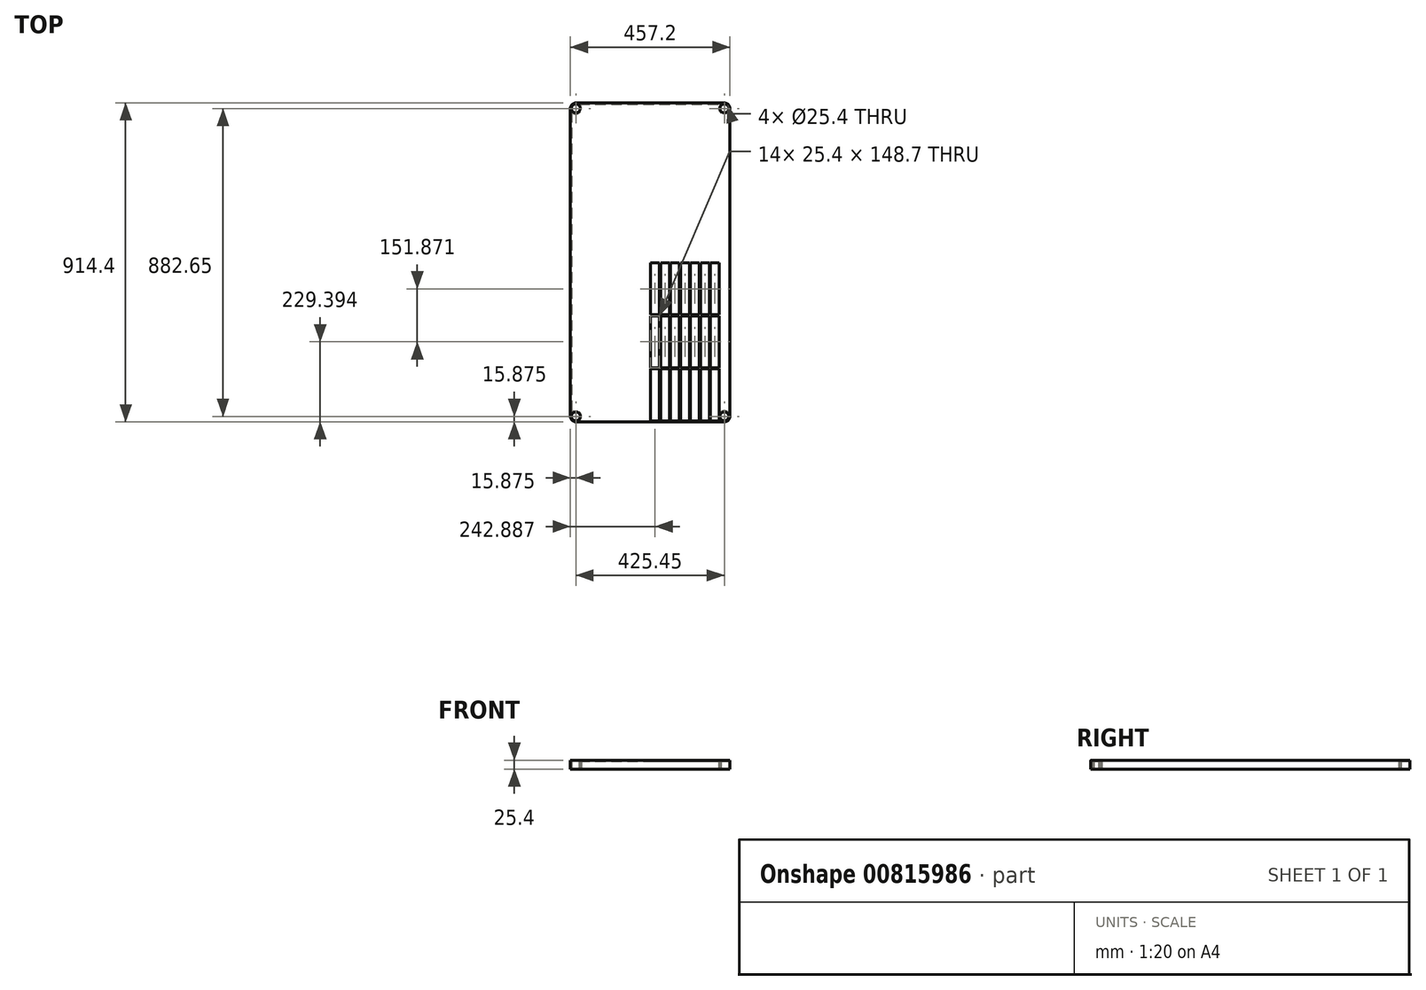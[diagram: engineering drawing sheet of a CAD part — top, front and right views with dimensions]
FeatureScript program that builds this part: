
annotation { "Feature Type Name" : "Feature", "Feature Type Description" : "" }
export const myFeature = defineFeature(function(context is Context, id is Id, definition is map)
    precondition{}
    {
        {
            var Q0;
            Q0=qCreatedBy(makeId("Top.planeOp"),FACE);
            var sketch = newSketch(context, id + "F0", { "sketchPlane" : qUnion([Q0])});
            skLineSegment(sketch, "E0.bottom", {"start": v(-212.73, 457.2) * mm, "end": v(212.72, 457.2) * mm});
            skLineSegment(sketch, "E0.top", {"start": v(-212.73, -457.2) * mm, "end": v(212.73, -457.2) * mm});
            skLineSegment(sketch, "E0.left", {"start": v(-228.6, 441.32) * mm, "end": v(-228.6, -441.33) * mm});
            skLineSegment(sketch, "E0.right", {"start": v(228.6, 441.33) * mm, "end": v(228.6, -441.33) * mm});
            skLineSegment(sketch, "E1", {"start": v(-228.6, 457.2) * mm, "end": v(228.6, -457.2) * mm, "construction": true});
            skPoint(sketch, "E2.visualSharp", {"position": v(-228.6, -457.2) * mm});
            skArc(sketch, "E2.filletArc", {"start": v(-228.6, -441.33) * mm, "mid": v(-223.95, -452.55) * mm, "end": v(-212.73, -457.2) * mm});
            skPoint(sketch, "E3.visualSharp", {"position": v(-228.6, 457.2) * mm});
            skArc(sketch, "E3.filletArc", {"start": v(-212.73, 457.2) * mm, "mid": v(-223.95, 452.55) * mm, "end": v(-228.6, 441.32) * mm});
            skPoint(sketch, "E4.visualSharp", {"position": v(228.6, 457.2) * mm});
            skArc(sketch, "E4.filletArc", {"start": v(228.6, 441.33) * mm, "mid": v(223.95, 452.55) * mm, "end": v(212.72, 457.2) * mm});
            skPoint(sketch, "E5.visualSharp", {"position": v(228.6, -457.2) * mm});
            skArc(sketch, "E5.filletArc", {"start": v(212.73, -457.2) * mm, "mid": v(223.95, -452.55) * mm, "end": v(228.6, -441.33) * mm});
            skCircle(sketch, "E6", {"center": v(-212.73, -441.33) * mm, "radius": 12.7 * mm});
            skCircle(sketch, "E7", {"center": v(212.73, -441.33) * mm, "radius": 12.7 * mm});
            skCircle(sketch, "E8", {"center": v(-212.73, 441.32) * mm, "radius": 12.7 * mm});
            skCircle(sketch, "E9", {"center": v(212.72, 441.33) * mm, "radius": 12.7 * mm});
            skSolve(sketch);
        }
        {
            var Q0;
            Q0=makeQuery(id+"F0.imprint","IMPRINT",FACE,{"disambiguationData":[TD([[makeQuery(id+"F0.imprint","IMPRINT",EDGE,{"derivedFrom":sQuery(id+"F0.wireOp",EDGE,"E0.bottom")}),-1.0]])]});
            extrude(context, id + "F1", {"entities" : qUnion([Q0]), "depth" : 25.4 * mm, "offsetDistance" : 25.4 * mm});
        }
        {
            var Q0;
            Q0=makeQuery(id+"F1.opExtrude","CAP_FACE",FACE,{"disambiguationData":[OSD([sQuery(id+"F0.wireOp",EDGE,"E0.bottom"),sQuery(id+"F0.wireOp",EDGE,"E0.top"),sQuery(id+"F0.wireOp",EDGE,"E0.left"),sQuery(id+"F0.wireOp",EDGE,"E0.right"),sQuery(id+"F0.wireOp",EDGE,"E2.filletArc"),sQuery(id+"F0.wireOp",EDGE,"E3.filletArc"),sQuery(id+"F0.wireOp",EDGE,"E4.filletArc"),sQuery(id+"F0.wireOp",EDGE,"E5.filletArc"),sQuery(id+"F0.wireOp",EDGE,"E6"),sQuery(id+"F0.wireOp",EDGE,"E7"),sQuery(id+"F0.wireOp",EDGE,"E8"),sQuery(id+"F0.wireOp",EDGE,"E9")])],"isStart":true});
            shell(context, id + "F2", {"entities" : qUnion([Q0]), "thickness" : 3.17 * mm});
        }
        {
            var Q0;
            Q0=makeQuery(id+"F1.opExtrude","CAP_FACE",FACE,{"disambiguationData":[OSD([sQuery(id+"F0.wireOp",EDGE,"E0.bottom"),sQuery(id+"F0.wireOp",EDGE,"E0.top"),sQuery(id+"F0.wireOp",EDGE,"E0.left"),sQuery(id+"F0.wireOp",EDGE,"E0.right"),sQuery(id+"F0.wireOp",EDGE,"E2.filletArc"),sQuery(id+"F0.wireOp",EDGE,"E3.filletArc"),sQuery(id+"F0.wireOp",EDGE,"E4.filletArc"),sQuery(id+"F0.wireOp",EDGE,"E5.filletArc"),sQuery(id+"F0.wireOp",EDGE,"E6"),sQuery(id+"F0.wireOp",EDGE,"E7"),sQuery(id+"F0.wireOp",EDGE,"E8"),sQuery(id+"F0.wireOp",EDGE,"E9")])],"isStart":false});
            var sketch = newSketch(context, id + "F3", { "sketchPlane" : qUnion([Q0])});
            skLineSegment(sketch, "E10.bottom", {"start": v(1.59, -1.59) * mm, "end": v(26.99, -1.59) * mm});
            skLineSegment(sketch, "E10.top", {"start": v(1.59, -150.28) * mm, "end": v(26.99, -150.28) * mm});
            skLineSegment(sketch, "E10.left", {"start": v(1.59, -1.59) * mm, "end": v(1.59, -150.28) * mm});
            skLineSegment(sketch, "E10.right", {"start": v(26.99, -1.59) * mm, "end": v(26.99, -150.28) * mm});
            skLineSegment(sketch, "E11.bottom", {"start": v(1.59, -153.46) * mm, "end": v(26.99, -153.46) * mm});
            skLineSegment(sketch, "E11.top", {"start": v(1.59, -302.15) * mm, "end": v(26.99, -302.15) * mm});
            skLineSegment(sketch, "E11.left", {"start": v(1.59, -153.46) * mm, "end": v(1.59, -302.15) * mm});
            skLineSegment(sketch, "E11.right", {"start": v(26.99, -153.46) * mm, "end": v(26.99, -302.15) * mm});
            skLineSegment(sketch, "E12.bottom", {"start": v(1.59, -305.33) * mm, "end": v(26.99, -305.33) * mm});
            skLineSegment(sketch, "E12.top", {"start": v(1.59, -454.03) * mm, "end": v(26.99, -454.03) * mm});
            skLineSegment(sketch, "E12.left", {"start": v(1.59, -305.33) * mm, "end": v(1.59, -454.03) * mm});
            skLineSegment(sketch, "E12.right", {"start": v(26.99, -305.33) * mm, "end": v(26.99, -454.03) * mm});
            skPoint(sketch, "E13", {"position": v(0, -457.2) * mm});
            skLineSegment(sketch, "E14.1.0.0", {"start": v(55.56, -153.46) * mm, "end": v(55.56, -302.15) * mm});
            skLineSegment(sketch, "E14.1.0.1", {"start": v(30.16, -1.59) * mm, "end": v(30.16, -150.28) * mm});
            skLineSegment(sketch, "E14.1.0.2", {"start": v(30.16, -153.46) * mm, "end": v(30.16, -302.15) * mm});
            skPoint(sketch, "E14.1.0.3", {"position": v(28.58, -457.2) * mm});
            skLineSegment(sketch, "E14.1.0.4", {"start": v(55.56, -305.33) * mm, "end": v(55.56, -454.03) * mm});
            skLineSegment(sketch, "E14.1.0.5", {"start": v(55.56, -1.59) * mm, "end": v(55.56, -150.28) * mm});
            skLineSegment(sketch, "E14.1.0.6", {"start": v(30.16, -305.33) * mm, "end": v(30.16, -454.03) * mm});
            skLineSegment(sketch, "E14.1.0.7", {"start": v(30.16, -454.03) * mm, "end": v(55.56, -454.03) * mm});
            skLineSegment(sketch, "E14.1.0.8", {"start": v(30.16, -1.59) * mm, "end": v(55.56, -1.59) * mm});
            skLineSegment(sketch, "E14.1.0.9", {"start": v(30.16, -305.33) * mm, "end": v(55.56, -305.33) * mm});
            skLineSegment(sketch, "E14.1.0.10", {"start": v(30.16, -302.15) * mm, "end": v(55.56, -302.15) * mm});
            skLineSegment(sketch, "E14.1.0.11", {"start": v(30.16, -150.28) * mm, "end": v(55.56, -150.28) * mm});
            skLineSegment(sketch, "E14.1.0.12", {"start": v(30.16, -153.46) * mm, "end": v(55.56, -153.46) * mm});
            skLineSegment(sketch, "E14.2.0.0", {"start": v(84.14, -153.46) * mm, "end": v(84.14, -302.15) * mm});
            skLineSegment(sketch, "E14.2.0.1", {"start": v(58.74, -1.59) * mm, "end": v(58.74, -150.28) * mm});
            skLineSegment(sketch, "E14.2.0.2", {"start": v(58.74, -153.46) * mm, "end": v(58.74, -302.15) * mm});
            skPoint(sketch, "E14.2.0.3", {"position": v(57.15, -457.2) * mm});
            skLineSegment(sketch, "E14.2.0.4", {"start": v(84.14, -305.33) * mm, "end": v(84.14, -454.03) * mm});
            skLineSegment(sketch, "E14.2.0.5", {"start": v(84.14, -1.59) * mm, "end": v(84.14, -150.28) * mm});
            skLineSegment(sketch, "E14.2.0.6", {"start": v(58.74, -305.33) * mm, "end": v(58.74, -454.03) * mm});
            skLineSegment(sketch, "E14.2.0.7", {"start": v(58.74, -454.03) * mm, "end": v(84.14, -454.03) * mm});
            skLineSegment(sketch, "E14.2.0.8", {"start": v(58.74, -1.59) * mm, "end": v(84.14, -1.59) * mm});
            skLineSegment(sketch, "E14.2.0.9", {"start": v(58.74, -305.33) * mm, "end": v(84.14, -305.33) * mm});
            skLineSegment(sketch, "E14.2.0.10", {"start": v(58.74, -302.15) * mm, "end": v(84.14, -302.15) * mm});
            skLineSegment(sketch, "E14.2.0.11", {"start": v(58.74, -150.28) * mm, "end": v(84.14, -150.28) * mm});
            skLineSegment(sketch, "E14.2.0.12", {"start": v(58.74, -153.46) * mm, "end": v(84.14, -153.46) * mm});
            skLineSegment(sketch, "E14.3.0.0", {"start": v(112.71, -153.46) * mm, "end": v(112.71, -302.15) * mm});
            skLineSegment(sketch, "E14.3.0.1", {"start": v(87.31, -1.59) * mm, "end": v(87.31, -150.28) * mm});
            skLineSegment(sketch, "E14.3.0.2", {"start": v(87.31, -153.46) * mm, "end": v(87.31, -302.15) * mm});
            skPoint(sketch, "E14.3.0.3", {"position": v(85.73, -457.2) * mm});
            skLineSegment(sketch, "E14.3.0.4", {"start": v(112.71, -305.33) * mm, "end": v(112.71, -454.03) * mm});
            skLineSegment(sketch, "E14.3.0.5", {"start": v(112.71, -1.59) * mm, "end": v(112.71, -150.28) * mm});
            skLineSegment(sketch, "E14.3.0.6", {"start": v(87.31, -305.33) * mm, "end": v(87.31, -454.03) * mm});
            skLineSegment(sketch, "E14.3.0.7", {"start": v(87.31, -454.03) * mm, "end": v(112.71, -454.03) * mm});
            skLineSegment(sketch, "E14.3.0.8", {"start": v(87.31, -1.59) * mm, "end": v(112.71, -1.59) * mm});
            skLineSegment(sketch, "E14.3.0.9", {"start": v(87.31, -305.33) * mm, "end": v(112.71, -305.33) * mm});
            skLineSegment(sketch, "E14.3.0.10", {"start": v(87.31, -302.15) * mm, "end": v(112.71, -302.15) * mm});
            skLineSegment(sketch, "E14.3.0.11", {"start": v(87.31, -150.28) * mm, "end": v(112.71, -150.28) * mm});
            skLineSegment(sketch, "E14.3.0.12", {"start": v(87.31, -153.46) * mm, "end": v(112.71, -153.46) * mm});
            skLineSegment(sketch, "E14.4.0.0", {"start": v(141.29, -153.46) * mm, "end": v(141.29, -302.15) * mm});
            skLineSegment(sketch, "E14.4.0.1", {"start": v(115.89, -1.59) * mm, "end": v(115.89, -150.28) * mm});
            skLineSegment(sketch, "E14.4.0.2", {"start": v(115.89, -153.46) * mm, "end": v(115.89, -302.15) * mm});
            skPoint(sketch, "E14.4.0.3", {"position": v(114.3, -457.2) * mm});
            skLineSegment(sketch, "E14.4.0.4", {"start": v(141.29, -305.33) * mm, "end": v(141.29, -454.03) * mm});
            skLineSegment(sketch, "E14.4.0.5", {"start": v(141.29, -1.59) * mm, "end": v(141.29, -150.28) * mm});
            skLineSegment(sketch, "E14.4.0.6", {"start": v(115.89, -305.33) * mm, "end": v(115.89, -454.03) * mm});
            skLineSegment(sketch, "E14.4.0.7", {"start": v(115.89, -454.03) * mm, "end": v(141.29, -454.03) * mm});
            skLineSegment(sketch, "E14.4.0.8", {"start": v(115.89, -1.59) * mm, "end": v(141.29, -1.59) * mm});
            skLineSegment(sketch, "E14.4.0.9", {"start": v(115.89, -305.33) * mm, "end": v(141.29, -305.33) * mm});
            skLineSegment(sketch, "E14.4.0.10", {"start": v(115.89, -302.15) * mm, "end": v(141.29, -302.15) * mm});
            skLineSegment(sketch, "E14.4.0.11", {"start": v(115.89, -150.28) * mm, "end": v(141.29, -150.28) * mm});
            skLineSegment(sketch, "E14.4.0.12", {"start": v(115.89, -153.46) * mm, "end": v(141.29, -153.46) * mm});
            skLineSegment(sketch, "E14.5.0.0", {"start": v(169.86, -153.46) * mm, "end": v(169.86, -302.15) * mm});
            skLineSegment(sketch, "E14.5.0.1", {"start": v(144.46, -1.59) * mm, "end": v(144.46, -150.28) * mm});
            skLineSegment(sketch, "E14.5.0.2", {"start": v(144.46, -153.46) * mm, "end": v(144.46, -302.15) * mm});
            skPoint(sketch, "E14.5.0.3", {"position": v(142.88, -457.2) * mm});
            skLineSegment(sketch, "E14.5.0.4", {"start": v(169.86, -305.33) * mm, "end": v(169.86, -454.03) * mm});
            skLineSegment(sketch, "E14.5.0.5", {"start": v(169.86, -1.59) * mm, "end": v(169.86, -150.28) * mm});
            skLineSegment(sketch, "E14.5.0.6", {"start": v(144.46, -305.33) * mm, "end": v(144.46, -454.03) * mm});
            skLineSegment(sketch, "E14.5.0.7", {"start": v(144.46, -454.03) * mm, "end": v(169.86, -454.03) * mm});
            skLineSegment(sketch, "E14.5.0.8", {"start": v(144.46, -1.59) * mm, "end": v(169.86, -1.59) * mm});
            skLineSegment(sketch, "E14.5.0.9", {"start": v(144.46, -305.33) * mm, "end": v(169.86, -305.33) * mm});
            skLineSegment(sketch, "E14.5.0.10", {"start": v(144.46, -302.15) * mm, "end": v(169.86, -302.15) * mm});
            skLineSegment(sketch, "E14.5.0.11", {"start": v(144.46, -150.28) * mm, "end": v(169.86, -150.28) * mm});
            skLineSegment(sketch, "E14.5.0.12", {"start": v(144.46, -153.46) * mm, "end": v(169.86, -153.46) * mm});
            skLineSegment(sketch, "E14.6.0.0", {"start": v(198.44, -153.46) * mm, "end": v(198.44, -302.15) * mm});
            skLineSegment(sketch, "E14.6.0.1", {"start": v(173.04, -1.59) * mm, "end": v(173.04, -150.28) * mm});
            skLineSegment(sketch, "E14.6.0.2", {"start": v(173.04, -153.46) * mm, "end": v(173.04, -302.15) * mm});
            skPoint(sketch, "E14.6.0.3", {"position": v(171.45, -457.2) * mm});
            skLineSegment(sketch, "E14.6.0.4", {"start": v(198.44, -305.33) * mm, "end": v(198.44, -454.03) * mm});
            skLineSegment(sketch, "E14.6.0.5", {"start": v(198.44, -1.59) * mm, "end": v(198.44, -150.28) * mm});
            skLineSegment(sketch, "E14.6.0.6", {"start": v(173.04, -305.33) * mm, "end": v(173.04, -454.03) * mm});
            skLineSegment(sketch, "E14.6.0.7", {"start": v(173.04, -454.03) * mm, "end": v(198.44, -454.03) * mm});
            skLineSegment(sketch, "E14.6.0.8", {"start": v(173.04, -1.59) * mm, "end": v(198.44, -1.59) * mm});
            skLineSegment(sketch, "E14.6.0.9", {"start": v(173.04, -305.33) * mm, "end": v(198.44, -305.33) * mm});
            skLineSegment(sketch, "E14.6.0.10", {"start": v(173.04, -302.15) * mm, "end": v(198.44, -302.15) * mm});
            skLineSegment(sketch, "E14.6.0.11", {"start": v(173.04, -150.28) * mm, "end": v(198.44, -150.28) * mm});
            skLineSegment(sketch, "E14.6.0.12", {"start": v(173.04, -153.46) * mm, "end": v(198.44, -153.46) * mm});
            skLineSegment(sketch, "E14.direction1", {"start": v(0, -457.2) * mm, "end": v(28.58, -457.2) * mm, "construction": true});
            skSolve(sketch);
        }
        {
            var Q0;
            Q0 = qSketchRegion(id + "F3", true);
            extrude(context, id + "F4", {"entities" : qUnion([Q0]), "operationType" : NewBodyOperationType.REMOVE, "endBound" : BoundingType.THROUGH_ALL, "oppositeDirection" : true, "depth" : 25.4 * mm, "offsetDistance" : 25.4 * mm});
        }
    });
